# Revit family: Trane_TVR_Indoor_Medium static pressure_4TVD0007(09,12)EF000AA(2nd DC)
name_source: partatom
category: Equipamento mecânico
units: mm (PartAtom-declared; Revit-internal decimal feet)

## family parameters
Com base no plano de trabalho = Não
Compartilhado = Não
Corte com vazios quando carregada = Não
Cota do conector redondo = Utilizar diâmetro
Número OmniClass = 23.75.00.00
Ponto de cálculo do ambiente = Não
Sempre na vertical = Sim
Tipo de parte = Normal
Título OmniClass = Climate Control (HVAC)

## types (3) — shared parameters
Condensation = air
Depth = 500  [stored 1.64042 ft]
Descrição = High efficiency air cooled
Fabricante = Trane
Gas = R410a
Gas pipe = 12.7  [stored 0.0416667 ft]
Height = 210
Installation = Indoor installation
Liquid pipe = 6.35  [stored 0.0208333 ft]
Machine material = grilles：ABS/HIPS
Maximum Fuse Amps = 15 A
Minimum Circuit Amps = 1 A
Net Weight = 18.00 kg
Power supply = 220-240V, 50/60Hz
Series = TVR ULTRA
URL = https://www.trane.com
Width = 780
clearance access left = 500  [stored 1.64042 ft]
clearance access right = 600
zero-valued in all types: clearance access behind, clearance access front

## per-type parameters (varying)
| type | Air  Flow | Cooling Capacity | Cooling Power Input | Heating Capacity | Heating Power Input |
| 4TVD0007EF000AA | 520/480/440/400/360/330/300 | 2.20 kW | 40 W | 2.60 kW | 40 W |
| 4TVD0009EF000AA | 520/480/440/400/360/330/300 | 2.80 kW | 40 W | 3.20 kW | 40 W |
| 4TVD0012EF000AA | 580/540/500/460/430/400/370 m3/h | 3.60 kW | 45 W | 4.00 kW | 45 W |

note: column(s) folded — value = type name in every type: Modelo

note: [stored X ft] marks values corroborated as IEEE doubles in the binary element streams (Revit-internal decimal feet)

## geometry (parser evidence)
native form markers: Sweep x5
no freeform markers — native parametric forms only
